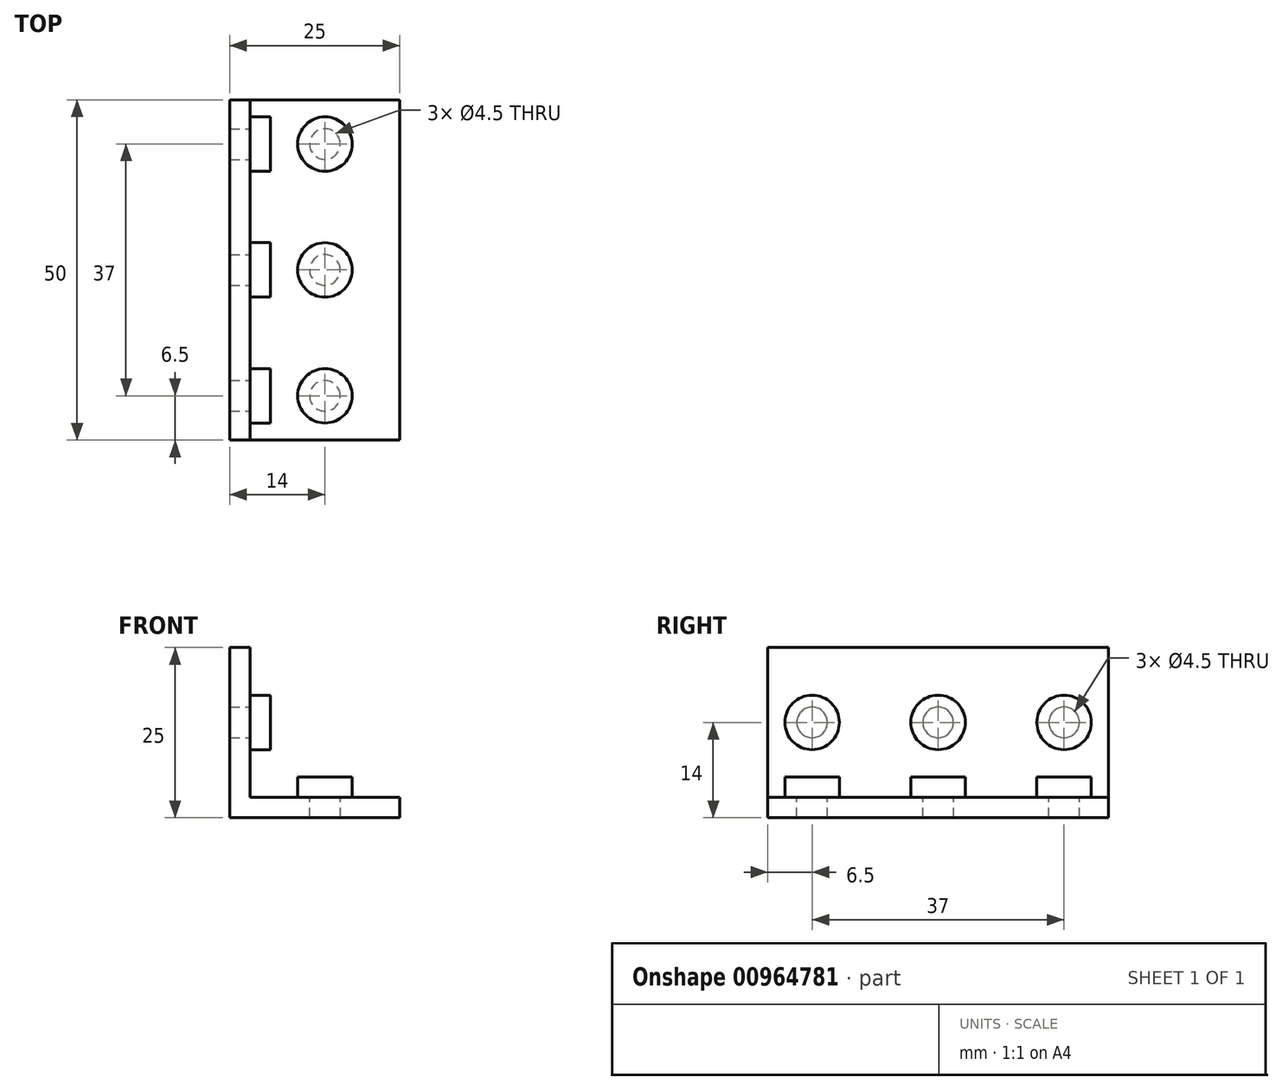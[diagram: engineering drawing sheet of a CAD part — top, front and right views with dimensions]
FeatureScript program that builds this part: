
annotation { "Feature Type Name" : "Feature", "Feature Type Description" : "" }
export const myFeature = defineFeature(function(context is Context, id is Id, definition is map)
    precondition{}
    {
        {
            assignVariable(context, id + "F0", {"name" : "Length", "anyValue" : 50});
        }
        {
            var Q0;
            Q0=qCreatedBy(makeId("Front.planeOp"),FACE);
            var sketch = newSketch(context, id + "F1", { "sketchPlane" : qUnion([Q0])});
            skLineSegment(sketch, "E0.bottom", {"start": v(0, 0) * mm, "end": v(25, 0) * mm});
            skLineSegment(sketch, "E0.top", {"start": v(0, 25) * mm, "end": v(25, 25) * mm});
            skLineSegment(sketch, "E0.left", {"start": v(0, 0) * mm, "end": v(0, 25) * mm});
            skLineSegment(sketch, "E0.right", {"start": v(25, 0) * mm, "end": v(25, 25) * mm});
            skLineSegment(sketch, "E1.bottom", {"start": v(25, 25) * mm, "end": v(3, 25) * mm});
            skLineSegment(sketch, "E1.top", {"start": v(25, 3) * mm, "end": v(3, 3) * mm});
            skLineSegment(sketch, "E1.left", {"start": v(25, 25) * mm, "end": v(25, 3) * mm});
            skLineSegment(sketch, "E1.right", {"start": v(3, 25) * mm, "end": v(3, 3) * mm});
            skSolve(sketch);
        }
        {
            var Q0;
            Q0=makeQuery(id+"F1.imprint","IMPRINT",FACE,{"disambiguationData":[TD([[makeQuery(id+"F1.imprint","IMPRINT",EDGE,{"derivedFrom":sQuery(id+"F1.wireOp",EDGE,"E0.bottom")}),1.0]])]});
            extrude(context, id + "F2", {"entities" : qUnion([Q0]), "depth" : (getVariable(context, 'Length')) * mm, "offsetDistance" : 25 * mm});
        }
        {
            var Q0;
            Q0=makeQuery(id+"F2.opExtrude","SWEPT_FACE",FACE,{"disambiguationData":[OSD([sQuery(id+"F1.wireOp",EDGE,"E1.right")])]});
            var sketch = newSketch(context, id + "F3", { "sketchPlane" : qUnion([Q0])});
            skLineSegment(sketch, "E2.0", {"start": v(-50, 25) * mm, "end": v(-50, 3) * mm});
            skLineSegment(sketch, "E2.1", {"start": v(-50, 25) * mm, "end": v(0, 25) * mm});
            skLineSegment(sketch, "E2.2", {"start": v(0, 25) * mm, "end": v(0, 3) * mm});
            skLineSegment(sketch, "E2.3", {"start": v(-50, 3) * mm, "end": v(0, 3) * mm});
            skLineSegment(sketch, "E3", {"start": v(-50, 14) * mm, "end": v(0, 14) * mm, "construction": true});
            skCircle(sketch, "E4", {"center": v(-43.5, 14) * mm, "radius": 2.25 * mm});
            skCircle(sketch, "E5", {"center": v(-43.5, 14) * mm, "radius": 4 * mm});
            skCircle(sketch, "E6", {"center": v(-43.5, 14) * mm, "radius": 6.5 * mm});
            skLineSegment(sketch, "E7", {"start": v(-43.5, 14) * mm, "end": v(-43.5, 3) * mm, "construction": true});
            skSolve(sketch);
        }
        {
            var Q0;
            Q0=makeQuery(id+"F2.opExtrude","SWEPT_FACE",FACE,{"disambiguationData":[OSD([sQuery(id+"F1.wireOp",EDGE,"E1.top")])]});
            var sketch = newSketch(context, id + "F4", { "sketchPlane" : qUnion([Q0])});
            skPoint(sketch, "E8.0", {"position": v(3, -43.5) * mm});
            skLineSegment(sketch, "E9.0", {"start": v(25, -50) * mm, "end": v(3, -50) * mm});
            skLineSegment(sketch, "E9.1", {"start": v(25, -50) * mm, "end": v(25, 0) * mm});
            skLineSegment(sketch, "E9.2", {"start": v(3, -50) * mm, "end": v(3, 0) * mm});
            skLineSegment(sketch, "E9.3", {"start": v(25, 0) * mm, "end": v(3, 0) * mm});
            skLineSegment(sketch, "E10", {"start": v(3, -43.5) * mm, "end": v(25, -43.5) * mm, "construction": true});
            skLineSegment(sketch, "E11", {"start": v(14, -50) * mm, "end": v(14, 0) * mm, "construction": true});
            skCircle(sketch, "E12", {"center": v(14, -43.5) * mm, "radius": 2.25 * mm});
            skCircle(sketch, "E13", {"center": v(14, -43.5) * mm, "radius": 4 * mm});
            skCircle(sketch, "E14", {"center": v(14, -43.5) * mm, "radius": 6.5 * mm});
            skCircle(sketch, "E15", {"center": v(14, -6.5) * mm, "radius": 2.25 * mm});
            skCircle(sketch, "E16", {"center": v(14, -6.5) * mm, "radius": 4 * mm});
            skCircle(sketch, "E17", {"center": v(14, -6.5) * mm, "radius": 6.5 * mm});
            skLineSegment(sketch, "E18", {"start": v(14, -6.5) * mm, "end": v(3, -6.5) * mm, "construction": true});
            skCircle(sketch, "E19", {"center": v(14, -25) * mm, "radius": 2.25 * mm});
            skCircle(sketch, "E20", {"center": v(14, -25) * mm, "radius": 4 * mm});
            skCircle(sketch, "E21", {"center": v(14, -25) * mm, "radius": 6.5 * mm});
            skLineSegment(sketch, "E22", {"start": v(14, -43.5) * mm, "end": v(14, -25) * mm});
            skLineSegment(sketch, "E23", {"start": v(14, -25) * mm, "end": v(14, -6.5) * mm});
            skSolve(sketch);
        }
        {
            var Q0;
            {var subQ0=sQuery(id+"F3.wireOp",EDGE,"E2.1");Q0=makeQuery(id+"F3.imprint","IMPRINT",FACE,{"disambiguationData":[TD([[makeQuery(id+"F3.imprint","IMPRINT",EDGE,{"derivedFrom":subQ0}),-1.0]])]});}
            var sketch = newSketch(context, id + "F5", { "sketchPlane" : qUnion([Q0])});
            skLineSegment(sketch, "E24.0", {"start": v(-50, 3) * mm, "end": v(0, 3) * mm});
            skLineSegment(sketch, "E24.1", {"start": v(0, 25) * mm, "end": v(0, 3) * mm});
            skLineSegment(sketch, "E24.2", {"start": v(-50, 25) * mm, "end": v(0, 25) * mm});
            skLineSegment(sketch, "E24.3", {"start": v(-50, 25) * mm, "end": v(-50, 3) * mm});
            skPoint(sketch, "E25.0", {"position": v(-6.5, 3) * mm});
            skLineSegment(sketch, "E26", {"start": v(-6.5, 3) * mm, "end": v(-6.5, 14) * mm, "construction": true});
            skCircle(sketch, "E27", {"center": v(-6.5, 14) * mm, "radius": 2.25 * mm});
            skCircle(sketch, "E28", {"center": v(-6.5, 14) * mm, "radius": 4 * mm});
            skCircle(sketch, "E29", {"center": v(-6.5, 14) * mm, "radius": 6.5 * mm});
            skCircle(sketch, "E30", {"center": v(-25, 14) * mm, "radius": 2.25 * mm});
            skCircle(sketch, "E31", {"center": v(-25, 14) * mm, "radius": 4 * mm});
            skCircle(sketch, "E32", {"center": v(-25, 14) * mm, "radius": 6.5 * mm});
            skPoint(sketch, "E33.0", {"position": v(-43.5, 14) * mm});
            skLineSegment(sketch, "E34.0", {"start": v(-50, 14) * mm, "end": v(0, 14) * mm, "construction": true});
            skLineSegment(sketch, "E35", {"start": v(-6.5, 14) * mm, "end": v(-25, 14) * mm, "construction": true});
            skLineSegment(sketch, "E36", {"start": v(-25, 14) * mm, "end": v(-43.5, 14) * mm, "construction": true});
            skSolve(sketch);
        }
        {
            var Q0;
            Q0=makeQuery(id+"F3.imprint","IMPRINT",FACE,{"disambiguationData":[TD([[makeQuery(id+"F3.imprint","IMPRINT",EDGE,{"derivedFrom":sQuery(id+"F3.wireOp",EDGE,"E4")}),1.0]])]});
            var Q1;
            Q1=makeQuery(id+"F5.imprint","IMPRINT",FACE,{"disambiguationData":[TD([[makeQuery(id+"F5.imprint","IMPRINT",EDGE,{"derivedFrom":sQuery(id+"F5.wireOp",EDGE,"E27")}),1.0]])]});
            var Q2;
            Q2=makeQuery(id+"F5.imprint","IMPRINT",FACE,{"disambiguationData":[TD([[makeQuery(id+"F5.imprint","IMPRINT",EDGE,{"derivedFrom":sQuery(id+"F5.wireOp",EDGE,"E30")}),1.0]])]});
            extrude(context, id + "F6", {"entities" : qUnion([Q0, Q1, Q2]), "operationType" : NewBodyOperationType.REMOVE, "endBound" : BoundingType.THROUGH_ALL, "oppositeDirection" : true, "depth" : 25 * mm, "offsetDistance" : 25 * mm});
        }
        {
            var Q0;
            Q0=makeQuery(id+"F4.imprint","IMPRINT",FACE,{"disambiguationData":[TD([[makeQuery(id+"F4.imprint","IMPRINT",EDGE,{"derivedFrom":sQuery(id+"F4.wireOp",EDGE,"E12")}),1.0]])]});
            var Q1;
            Q1=makeQuery(id+"F4.imprint","IMPRINT",FACE,{"disambiguationData":[TD([[makeQuery(id+"F4.imprint","IMPRINT",EDGE,{"derivedFrom":sQuery(id+"F4.wireOp",EDGE,"E15")}),1.0]])]});
            var Q2;
            Q2=makeQuery(id+"F4.imprint","IMPRINT",FACE,{"disambiguationData":[TD([[makeQuery(id+"F4.imprint","IMPRINT",EDGE,{"derivedFrom":sQuery(id+"F4.wireOp",EDGE,"E19")}),1.0]])]});
            extrude(context, id + "F7", {"entities" : qUnion([Q0, Q1, Q2]), "operationType" : NewBodyOperationType.REMOVE, "endBound" : BoundingType.THROUGH_ALL, "oppositeDirection" : true, "depth" : 25 * mm, "offsetDistance" : 25 * mm});
        }
        {
            var Q0;
            Q0=makeQuery(id+"F4.imprint","IMPRINT",FACE,{"disambiguationData":[TD([[makeQuery(id+"F4.imprint","IMPRINT",EDGE,{"derivedFrom":sQuery(id+"F4.wireOp",EDGE,"E15")}),-1.0]])]});
            var Q1;
            Q1=makeQuery(id+"F4.imprint","IMPRINT",FACE,{"disambiguationData":[TD([[makeQuery(id+"F4.imprint","IMPRINT",EDGE,{"derivedFrom":sQuery(id+"F4.wireOp",EDGE,"E15")}),1.0]])]});
            var Q2;
            {var subQ0=sQuery(id+"F4.wireOp",EDGE,"E22");var subQ1=sQuery(id+"F4.wireOp",EDGE,"E19");var subQ2=makeQuery(id+"F4.imprint","INTERSECT",VERTEX,{"derivedFrom":[subQ1,subQ0]});Q2=makeQuery(id+"F4.imprint","IMPRINT",FACE,{"disambiguationData":[TD([[makeQuery(id+"F4.imprint","IMPRINT",EDGE,{"disambiguationData":[TD([[subQ2,-1.0]])],"derivedFrom":subQ1}),-1.0]])]});}
            var Q3;
            {var subQ0=sQuery(id+"F4.wireOp",EDGE,"E22");var subQ1=sQuery(id+"F4.wireOp",EDGE,"E19");var subQ2=makeQuery(id+"F4.imprint","INTERSECT",VERTEX,{"derivedFrom":[subQ1,subQ0]});Q3=makeQuery(id+"F4.imprint","IMPRINT",FACE,{"disambiguationData":[TD([[makeQuery(id+"F4.imprint","IMPRINT",EDGE,{"disambiguationData":[TD([[subQ2,1.0]])],"derivedFrom":subQ1}),-1.0]])]});}
            var Q4;
            {var subQ0=sQuery(id+"F4.wireOp",EDGE,"E22");var subQ1=sQuery(id+"F4.wireOp",EDGE,"E19");var subQ2=makeQuery(id+"F4.imprint","INTERSECT",VERTEX,{"derivedFrom":[subQ1,subQ0]});Q4=makeQuery(id+"F4.imprint","IMPRINT",FACE,{"disambiguationData":[TD([[makeQuery(id+"F4.imprint","IMPRINT",EDGE,{"disambiguationData":[TD([[subQ2,-1.0]])],"derivedFrom":subQ1}),1.0]])]});}
            var Q5;
            {var subQ0=sQuery(id+"F4.wireOp",EDGE,"E22");var subQ1=sQuery(id+"F4.wireOp",EDGE,"E19");var subQ2=makeQuery(id+"F4.imprint","INTERSECT",VERTEX,{"derivedFrom":[subQ1,subQ0]});Q5=makeQuery(id+"F4.imprint","IMPRINT",FACE,{"disambiguationData":[TD([[makeQuery(id+"F4.imprint","IMPRINT",EDGE,{"disambiguationData":[TD([[subQ2,1.0]])],"derivedFrom":subQ1}),1.0]])]});}
            var Q6;
            Q6=makeQuery(id+"F4.imprint","IMPRINT",FACE,{"disambiguationData":[TD([[makeQuery(id+"F4.imprint","IMPRINT",EDGE,{"derivedFrom":sQuery(id+"F4.wireOp",EDGE,"E12")}),-1.0]])]});
            var Q7;
            Q7=makeQuery(id+"F4.imprint","IMPRINT",FACE,{"disambiguationData":[TD([[makeQuery(id+"F4.imprint","IMPRINT",EDGE,{"derivedFrom":sQuery(id+"F4.wireOp",EDGE,"E12")}),1.0]])]});
            extrude(context, id + "F8", {"entities" : qUnion([Q0, Q1, Q2, Q3, Q4, Q5, Q6, Q7]), "depth" : 3 * mm, "offsetDistance" : 25 * mm});
        }
        {
            var Q0;
            Q0=makeQuery(id+"F5.imprint","IMPRINT",FACE,{"disambiguationData":[TD([[makeQuery(id+"F5.imprint","IMPRINT",EDGE,{"derivedFrom":sQuery(id+"F5.wireOp",EDGE,"E27")}),-1.0]])]});
            var Q1;
            Q1=makeQuery(id+"F5.imprint","IMPRINT",FACE,{"disambiguationData":[TD([[makeQuery(id+"F5.imprint","IMPRINT",EDGE,{"derivedFrom":sQuery(id+"F5.wireOp",EDGE,"E27")}),1.0]])]});
            var Q2;
            Q2=makeQuery(id+"F5.imprint","IMPRINT",FACE,{"disambiguationData":[TD([[makeQuery(id+"F5.imprint","IMPRINT",EDGE,{"derivedFrom":sQuery(id+"F5.wireOp",EDGE,"E30")}),-1.0]])]});
            var Q3;
            Q3=makeQuery(id+"F5.imprint","IMPRINT",FACE,{"disambiguationData":[TD([[makeQuery(id+"F5.imprint","IMPRINT",EDGE,{"derivedFrom":sQuery(id+"F5.wireOp",EDGE,"E30")}),1.0]])]});
            var Q4;
            Q4=makeQuery(id+"F3.imprint","IMPRINT",FACE,{"disambiguationData":[TD([[makeQuery(id+"F3.imprint","IMPRINT",EDGE,{"derivedFrom":sQuery(id+"F3.wireOp",EDGE,"E4")}),-1.0]])]});
            var Q5;
            Q5=makeQuery(id+"F3.imprint","IMPRINT",FACE,{"disambiguationData":[TD([[makeQuery(id+"F3.imprint","IMPRINT",EDGE,{"derivedFrom":sQuery(id+"F3.wireOp",EDGE,"E4")}),1.0]])]});
            extrude(context, id + "F9", {"entities" : qUnion([Q0, Q1, Q2, Q3, Q4, Q5]), "depth" : 3 * mm, "offsetDistance" : 25 * mm});
        }
    });
